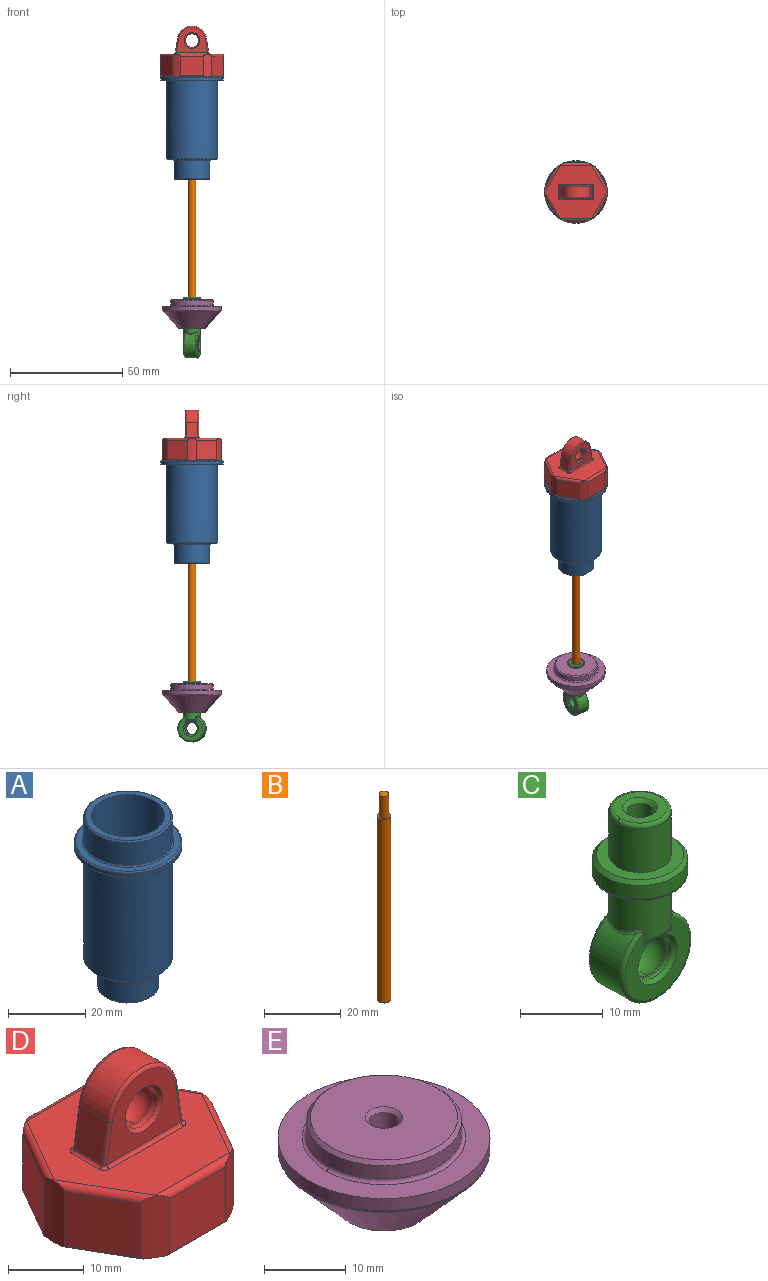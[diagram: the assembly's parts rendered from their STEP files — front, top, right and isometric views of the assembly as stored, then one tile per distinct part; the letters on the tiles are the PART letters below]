
ASSEMBLY  parts=5 mates=4
PART A: 28 faces, bbox 28x28x54.1 mm
  f0: torus R=9.1mm, axis (0,0,-1), area 18.5mm2, adj f4,f18,f19
  f1: torus R=11.9mm, axis (0,0,-1), area 23mm2, adj f6,f20,f22
  f2: torus R=5.6mm, axis (0,0,-1), area 11.6mm2, adj f9,f21,f23
  f3: torus R=8.4mm, axis (0,0,-1), area 16.1mm2, adj f15,f26,f27
  f4: cylinder r=9.5mm len=42.6mm, axis (0,0,-1), area 2542.8mm2, adj f0,f17,f18
  f5: cone r=11.5mm half-angle=45deg, axis (0,0,-1), area 40.2mm2, adj f6,f17
  f6: cylinder r=11.5mm len=23mm, axis (0,0,-1), area 520.2mm2, adj f1,f5,f20
  f7: cylinder r=3.78mm len=7.56mm, axis (0,0,-1), area 49.9mm2, adj f19,f21
  f8: cone r=14mm half-angle=45deg, axis (0,0,-1), area 49mm2, adj f10,f22
  f9: cylinder r=6mm len=12mm, axis (0,0,-1), area 309.1mm2, adj f2,f11,f23
  f10: cylinder r=14mm len=28mm, axis (0,0,-1), area 105.6mm2, adj f8,f12
  f11: cone r=6.4mm half-angle=45deg, axis (0,0,-1), area 22mm2, adj f9,f24
  f12: cone r=14mm half-angle=45deg, axis (0,0,1), area 49mm2, adj f10,f25
  f13: cone r=8mm half-angle=45deg, axis (0,0,1), area 27.7mm2, adj f15,f24
  f14: cylinder r=11.5mm len=34.7mm, axis (0,0,-1), area 2507.3mm2, adj f16,f25
  f15: cylinder r=8mm len=16mm, axis (0,0,-1), area 412.2mm2, adj f3,f13,f26
  f16: cone r=11.5mm half-angle=45deg, axis (0,0,1), area 40.2mm2, adj f14,f27
  f17: plane 22.2x22.2mm, normal (0,0,1), area 103.5mm2, adj f4,f5
  f18: torus R=9.1mm, axis (0,0,-1), area 18.5mm2, adj f0,f4,f19
  f19: plane 18.2x18.2mm, normal (0,0,1), area 215.3mm2, adj f0,f7,f18
  f20: torus R=11.9mm, axis (0,0,-1), area 23mm2, adj f1,f6,f22
  f21: plane 11.2x11.2mm, normal (0,0,-1), area 53.6mm2, adj f2,f7,f23
  f22: plane 27.2x27.2mm, normal (0,0,1), area 136.2mm2, adj f1,f8,f20
  f23: torus R=5.6mm, axis (0,0,-1), area 11.6mm2, adj f2,f9,f21
  f24: plane 15.2x15.2mm, normal (0,0,-1), area 52.8mm2, adj f11,f13
  f25: plane 27.2x27.2mm, normal (0,0,-1), area 165.6mm2, adj f12,f14
  f26: torus R=8.4mm, axis (0,0,-1), area 16.1mm2, adj f3,f15,f27
  f27: plane 22.2x22.2mm, normal (0,0,-1), area 165.4mm2, adj f3,f16,f26
PART B: 5 faces, bbox 3.6x3.6x65.5 mm
  f0: cylinder r=1.78mm len=58.5mm, axis (0,0,-1), area 654.3mm2, adj f2,f3
  f1: cylinder r=1.3mm len=7mm, axis (0,0,-1), area 57.2mm2, adj f3,f4
  f2: plane 3.56x3.56mm, normal (0,0,-1), area 10mm2, adj f0
  f3: plane 3.56x3.56mm, normal (0,0,1), area 4.6mm2, adj f0,f1
  f4: plane 2.6x2.6mm, normal (0,0,1), area 5.3mm2, adj f1
PART C: 54 faces, bbox 13x12.5x27.5 mm
  f0: torus R=4.29mm, axis (0,0,1), area 9.8mm2, adj f5,f28,f42
  f1: torus R=5.29mm, axis (0,0,1), area 13.8mm2, adj f11,f42,f46
  f2: sphere r=3.4mm, area 35.6mm2, adj f10,f47,f49
  f3: torus R=3.29mm, axis (0,0,1), area 8.9mm2, adj f13,f51,f52
  f4: cylinder r=6mm len=12mm, axis (0,-1,0), area 148.5mm2, adj f16,f17,f18,f19,f20,f21
  f5: cylinder r=3.79mm len=7.57mm, axis (0,0,1), area 140.6mm2, adj f0,f17,f18,f20,f21,f24,f25,f26
  f6: cone r=3.4mm half-angle=45deg, axis (0,-1,0), area 12.4mm2, adj f8,f22,f32,f33
  f7: cone r=3.4mm half-angle=45deg, axis (0,1,0), area 12.4mm2, adj f9,f23,f43,f44
  f8: cylinder r=2.9mm len=5.8mm, axis (0,-1,0), area 10.8mm2, adj f6,f10,f32,f33
  f9: cylinder r=2.9mm len=5.8mm, axis (0,-1,0), area 10.8mm2, adj f7,f43,f44,f47,f48
  f10: cone r=2.96mm half-angle=14.7deg, axis (0,1,0), area 4.7mm2, adj f2,f8,f49
  f11: cylinder r=5.79mm len=11.57mm, axis (0,0,1), area 72.7mm2, adj f1,f12,f46
  f12: cone r=5.79mm half-angle=45deg, axis (0,0,-1), area 24.6mm2, adj f11,f50
  f13: cylinder r=3.79mm len=7.57mm, axis (0,0,1), area 154.6mm2, adj f3,f50,f51
  f14: cone r=2.1mm half-angle=45deg, axis (0,0,1), area 8.2mm2, adj f15,f52
  f15: cylinder r=1.6mm len=14.5mm, axis (0,0,1), area 145.8mm2, adj f14,f53
  f16: torus R=5.5mm, axis (0,-1,0), area 24.2mm2, adj f4,f22,f40,f41
  f17: bspline ~1.43x0.89mm, area 0.7mm2, adj f4,f5,f18,f41
  f18: bspline ~3.74x1.06mm, area 1.9mm2, adj f4,f5,f17,f27
  f19: torus R=5.5mm, axis (0,-1,0), area 24.2mm2, adj f4,f23,f27,f29
  f20: bspline ~3.78x1.11mm, area 1.9mm2, adj f4,f5,f21,f29
  f21: bspline ~1.41x0.89mm, area 0.7mm2, adj f4,f5,f20,f40
  f22: plane 11x10.42mm, normal (0,-1,0), area 48.5mm2, adj f6,f16,f24,f25,f45
  f23: plane 11x10.42mm, normal (0,1,0), area 48.5mm2, adj f7,f19,f30,f31,f37
  f24: cylinder r=0.5mm len=1.74mm, axis (0,0,-1), area 0.4mm2, adj f5,f22,f34,f41
  f25: cylinder r=0.5mm len=1.74mm, axis (0,0,1), area 0.4mm2, adj f5,f22,f35,f40
  f26: bspline ~4.55x0.85mm, area 2.5mm2, adj f5,f36,f37,f38
  f27: bspline ~1.2x1.09mm, area 0.6mm2, adj f5,f18,f19,f30
  f28: torus R=4.29mm, axis (0,0,1), area 9.8mm2, adj f0,f5,f42
  f29: bspline ~1.19x1.08mm, area 0.6mm2, adj f5,f19,f20,f31
  f30: cylinder r=0.5mm len=1.74mm, axis (0,0,1), area 0.4mm2, adj f5,f23,f27,f38
  f31: cylinder r=0.5mm len=1.74mm, axis (0,0,-1), area 0.4mm2, adj f5,f23,f29,f36
  f32: bspline ~1.4x0.63mm, area 0.8mm2, adj f6,f8,f33,f45
  f33: bspline ~1.4x0.63mm, area 0.8mm2, adj f6,f8,f32,f45
  f34: bspline ~0.84x0.58mm, area 0.1mm2, adj f24,f39,f45
  f35: bspline ~0.84x0.58mm, area 0.1mm2, adj f25,f39,f45
  f36: bspline ~0.84x0.58mm, area 0.1mm2, adj f26,f31,f37
  f37: cylinder r=0.5mm len=4.94mm, axis (1,0,0), area 2.2mm2, adj f23,f26,f36,f38,f43,f44
  f38: bspline ~0.84x0.58mm, area 0.1mm2, adj f26,f30,f37
  f39: bspline ~4.55x0.87mm, area 2.5mm2, adj f5,f34,f35,f45
  f40: bspline ~1.2x1.09mm, area 0.6mm2, adj f5,f16,f21,f25
  f41: bspline ~1.2x1.09mm, area 0.6mm2, adj f5,f16,f17,f24
  f42: plane 10.57x10.57mm, normal (0,0,-1), area 30.1mm2, adj f0,f1,f28,f46
  f43: bspline ~1.4x0.63mm, area 0.8mm2, adj f7,f9,f37,f44
  f44: bspline ~1.43x0.63mm, area 0.8mm2, adj f7,f9,f37,f43
  f45: cylinder r=0.5mm len=4.94mm, axis (-1,0,0), area 2.2mm2, adj f22,f32,f33,f34,f35,f39
  f46: torus R=5.29mm, axis (0,0,1), area 13.8mm2, adj f1,f11,f42
  f47: cone r=2.96mm half-angle=14.7deg, axis (0,-1,0), area 2.3mm2, adj f2,f9,f48
  f48: cone r=2.96mm half-angle=14.7deg, axis (0,-1,0), area 2.3mm2, adj f9,f47,f49
  f49: sphere r=3.4mm, area 35.6mm2, adj f2,f10,f48
  f50: plane 10.57x10.57mm, normal (0,0,1), area 42.7mm2, adj f12,f13
  f51: torus R=3.29mm, axis (0,0,1), area 8.9mm2, adj f3,f13,f52
  f52: plane 6.57x6.57mm, normal (0,0,1), area 20.1mm2, adj f3,f14,f51
  f53: plane 3.2x3.2mm, normal (0,0,1), area 8mm2, adj f15
PART D: 56 faces, bbox 29.6x26.1x23.1 mm
  f0: sphere r=3.4mm, area 33.8mm2, adj f4,f5,f53
  f1: torus R=10.05mm, axis (0,0,-1), area 10mm2, adj f7,f54,f55
  f2: cone r=3.51mm half-angle=45deg, axis (0,-1,0), area 14.5mm2, adj f4,f23
  f3: cone r=3.51mm half-angle=45deg, axis (0,1,0), area 14.5mm2, adj f5,f25
  f4: cylinder r=3.01mm len=6.02mm, axis (0,1,0), area 17.4mm2, adj f0,f2,f53
  f5: cylinder r=3.01mm len=6.02mm, axis (0,1,0), area 17.4mm2, adj f0,f3,f53
  f6: cone r=10.75mm half-angle=45deg, axis (0,0,-1), area 46.7mm2, adj f7,f46
  f7: cylinder r=10.25mm len=20.5mm, axis (0,0,-1), area 470.1mm2, adj f1,f6,f54
  f8: plane 27.77x24.06mm, normal (0,0,1), area 388.7mm2, adj f9,f10,f11,f12,f13,f14,f15,f16
  f9: bspline ~1.09x1.01mm, area 0.8mm2, adj f8,f10,f16,f41
  f10: cylinder r=0.5mm len=13.85mm, axis (1,0,0), area 10.9mm2, adj f8,f9,f11,f23
  f11: bspline ~1.09x1.02mm, area 0.8mm2, adj f8,f10,f12,f39
  f12: cylinder r=0.5mm len=5mm, axis (0,-1,0), area 3.5mm2, adj f8,f11,f13,f24
  f13: bspline ~1.09x1.01mm, area 0.8mm2, adj f8,f12,f14,f42
  f14: cylinder r=0.5mm len=13.85mm, axis (-1,0,0), area 10.9mm2, adj f8,f13,f15,f25
  f15: bspline ~1.09x1.02mm, area 0.8mm2, adj f8,f14,f16,f45
  f16: cylinder r=0.5mm len=5mm, axis (0,-1,0), area 3.5mm2, adj f8,f9,f15,f26
  f17: cylinder r=1mm len=14mm, axis (-1,0,0), area 18.8mm2, adj f8,f18,f22,f27,f28,f29
  f18: cylinder r=1mm len=12.62mm, axis (-0.5,-0.87,0), area 18.8mm2, adj f8,f17,f19,f28,f30,f31
  f19: cylinder r=1mm len=12.62mm, axis (0.5,-0.87,0), area 18.8mm2, adj f8,f18,f20,f30,f32,f33
  f20: cylinder r=1mm len=14mm, axis (1,0,0), area 18.8mm2, adj f8,f19,f21,f32,f34,f35
  f21: cylinder r=1mm len=12.62mm, axis (0.5,0.87,0), area 18.8mm2, adj f8,f20,f22,f34,f36,f37
  f22: cylinder r=1mm len=12.62mm, axis (-0.5,0.87,0), area 18.8mm2, adj f8,f17,f21,f27,f36,f38
  f23: plane 13.84x11.5mm, normal (0,-1,0), area 89.3mm2, adj f2,f10,f39,f40,f41
  f24: plane 6.57x5mm, normal (-0.99,0,0.15), area 33.2mm2, adj f12,f39,f42,f43
  f25: plane 13.83x11.5mm, normal (0,1,0), area 89.3mm2, adj f3,f14,f42,f44,f45
  f26: plane 6.57x5mm, normal (0.99,0,0.15), area 33.2mm2, adj f16,f41,f43,f45
  f27: cylinder r=14mm len=9.99mm, axis (0,0,-1), area 39mm2, adj f17,f22,f29,f38,f46,f47,f52
  f28: cylinder r=14mm len=9.99mm, axis (0,0,-1), area 39mm2, adj f17,f18,f29,f31,f46,f47,f48
  f29: plane 10.39x8.8mm, normal (0,1,0), area 91.5mm2, adj f17,f27,f28,f47
  f30: cylinder r=14mm len=9.99mm, axis (0,0,-1), area 39mm2, adj f18,f19,f31,f33,f46,f48,f49
  f31: plane 9x8.8mm, normal (-0.87,0.5,0), area 91.5mm2, adj f18,f28,f30,f48
  f32: cylinder r=14mm len=9.99mm, axis (0,0,-1), area 39mm2, adj f19,f20,f33,f35,f46,f49,f50
  f33: plane 9x8.8mm, normal (-0.87,-0.5,0), area 91.5mm2, adj f19,f30,f32,f49
  f34: cylinder r=14mm len=9.99mm, axis (0,0,-1), area 39mm2, adj f20,f21,f35,f37,f46,f50,f51
  f35: plane 10.39x8.8mm, normal (0,-1,0), area 91.5mm2, adj f20,f32,f34,f50
  f36: cylinder r=14mm len=9.99mm, axis (0,0,-1), area 39mm2, adj f21,f22,f37,f38,f46,f51,f52
  f37: plane 9x8.8mm, normal (0.87,-0.5,0), area 91.5mm2, adj f21,f34,f36,f51
  f38: plane 9x8.8mm, normal (0.87,0.5,0), area 91.5mm2, adj f22,f27,f36,f52
  f39: cylinder r=0.5mm len=6.64mm, axis (-0.15,0,-0.99), area 5.2mm2, adj f11,f23,f24,f40
  f40: torus R=6mm, axis (0,-1,0), area 14.1mm2, adj f23,f39,f41,f43
  f41: cylinder r=0.5mm len=6.64mm, axis (-0.15,0,0.99), area 5.2mm2, adj f9,f23,f26,f40
  f42: cylinder r=0.5mm len=6.64mm, axis (0.15,0,0.99), area 5.2mm2, adj f13,f24,f25,f44
  f43: cylinder r=6.5mm len=12.85mm, axis (0,-1,0), area 92.2mm2, adj f24,f26,f40,f44
  f44: torus R=6mm, axis (0,-1,0), area 14.1mm2, adj f25,f42,f43,f45
  f45: cylinder r=0.5mm len=6.64mm, axis (0.15,0,-0.99), area 5.2mm2, adj f15,f25,f26,f44
  f46: plane 28x25.6mm, normal (0,0,-1), area 197.8mm2, adj f6,f27,f28,f30,f32,f34,f36,f47
  f47: cylinder r=0.2mm len=11.34mm, axis (1,0,0), area 3.4mm2, adj f27,f28,f29,f46
  f48: cylinder r=0.2mm len=9.92mm, axis (0.5,0.87,0), area 3.4mm2, adj f28,f30,f31,f46
  f49: cylinder r=0.2mm len=9.92mm, axis (-0.5,0.87,0), area 3.4mm2, adj f30,f32,f33,f46
  f50: cylinder r=0.2mm len=11.34mm, axis (-1,0,0), area 3.4mm2, adj f32,f34,f35,f46
  f51: cylinder r=0.2mm len=9.92mm, axis (-0.5,-0.87,0), area 3.4mm2, adj f34,f36,f37,f46
  f52: cylinder r=0.2mm len=9.92mm, axis (0.5,-0.87,0), area 3.4mm2, adj f27,f36,f38,f46
  f53: sphere r=3.4mm, area 33.8mm2, adj f0,f4,f5
  f54: torus R=10.05mm, axis (0,0,-1), area 10mm2, adj f1,f7,f55
  f55: plane 20.1x20.1mm, normal (0,0,-1), area 317.3mm2, adj f1,f54
PART E: 18 faces, bbox 28.1x28.1x13 mm
  f0: torus R=5.55mm, axis (0,0,1), area 7.5mm2, adj f3,f11,f13
  f1: torus R=12.5mm, axis (0,0,1), area 15mm2, adj f3,f4,f12
  f2: torus R=10.02mm, axis (0,0,1), area 23.9mm2, adj f7,f14,f15
  f3: cone r=12.87mm half-angle=42.1deg, axis (0,0,1), area 612.1mm2, adj f0,f1,f11,f12
  f4: cylinder r=13mm len=26mm, axis (0,0,1), area 147.5mm2, adj f1,f12,f14
  f5: cone r=4.27mm half-angle=45deg, axis (0,0,-1), area 17.9mm2, adj f6,f13
  f6: cylinder r=3.77mm len=7.54mm, axis (0,0,1), area 154mm2, adj f5,f16
  f7: cylinder r=9.53mm len=19.05mm, axis (0,0,1), area 119.7mm2, adj f2,f9,f15
  f8: cone r=1.8mm half-angle=0deg, axis (0,0,1), area 62.3mm2, adj f10,f16
  f9: cone r=9.53mm half-angle=45deg, axis (0,0,-1), area 41.2mm2, adj f7,f17
  f10: cone r=2.31mm half-angle=45deg, axis (0,0,1), area 9.1mm2, adj f8,f17
  f11: torus R=5.55mm, axis (0,0,1), area 7.5mm2, adj f0,f3,f13
  f12: torus R=12.5mm, axis (0,0,1), area 15mm2, adj f1,f3,f4
  f13: plane 11.1x11.1mm, normal (0,0,-1), area 39.4mm2, adj f0,f5,f11
  f14: plane 26x26mm, normal (0,0,1), area 215.2mm2, adj f2,f4,f15
  f15: torus R=10.02mm, axis (0,0,1), area 23.9mm2, adj f2,f7,f14
  f16: plane 7.54x7.54mm, normal (0,0,-1), area 34.5mm2, adj f6,f8
  f17: plane 18.05x18.05mm, normal (0,0,1), area 239.2mm2, adj f9,f10
PLACE A at identity
PLACE B rot(axis=(0,0,1),90deg) t=(0,0,-10.5)mm
PLACE C rot(axis=(0,0,-1),100.4deg) t=(0,0,-135.53)mm
PLACE D at identity
PLACE E rot(axis=(0,0,-1),141.8deg) t=(0,0,-149.77)mm
MATE revolute B.f0 <-> E.f11  axis (0,0,-1) through (0,0,-120.5)mm
MATE cylindrical B.f0 <-> A.f20  axis (0,0,1) through (0,0,-62)mm
MATE revolute D.f6 <-> A.f18  axis (0,0,-1) through (0,0,-16)mm
MATE revolute C.f0 <-> E.f11  axis (0,0,1) through (0,0,-121.5)mm
